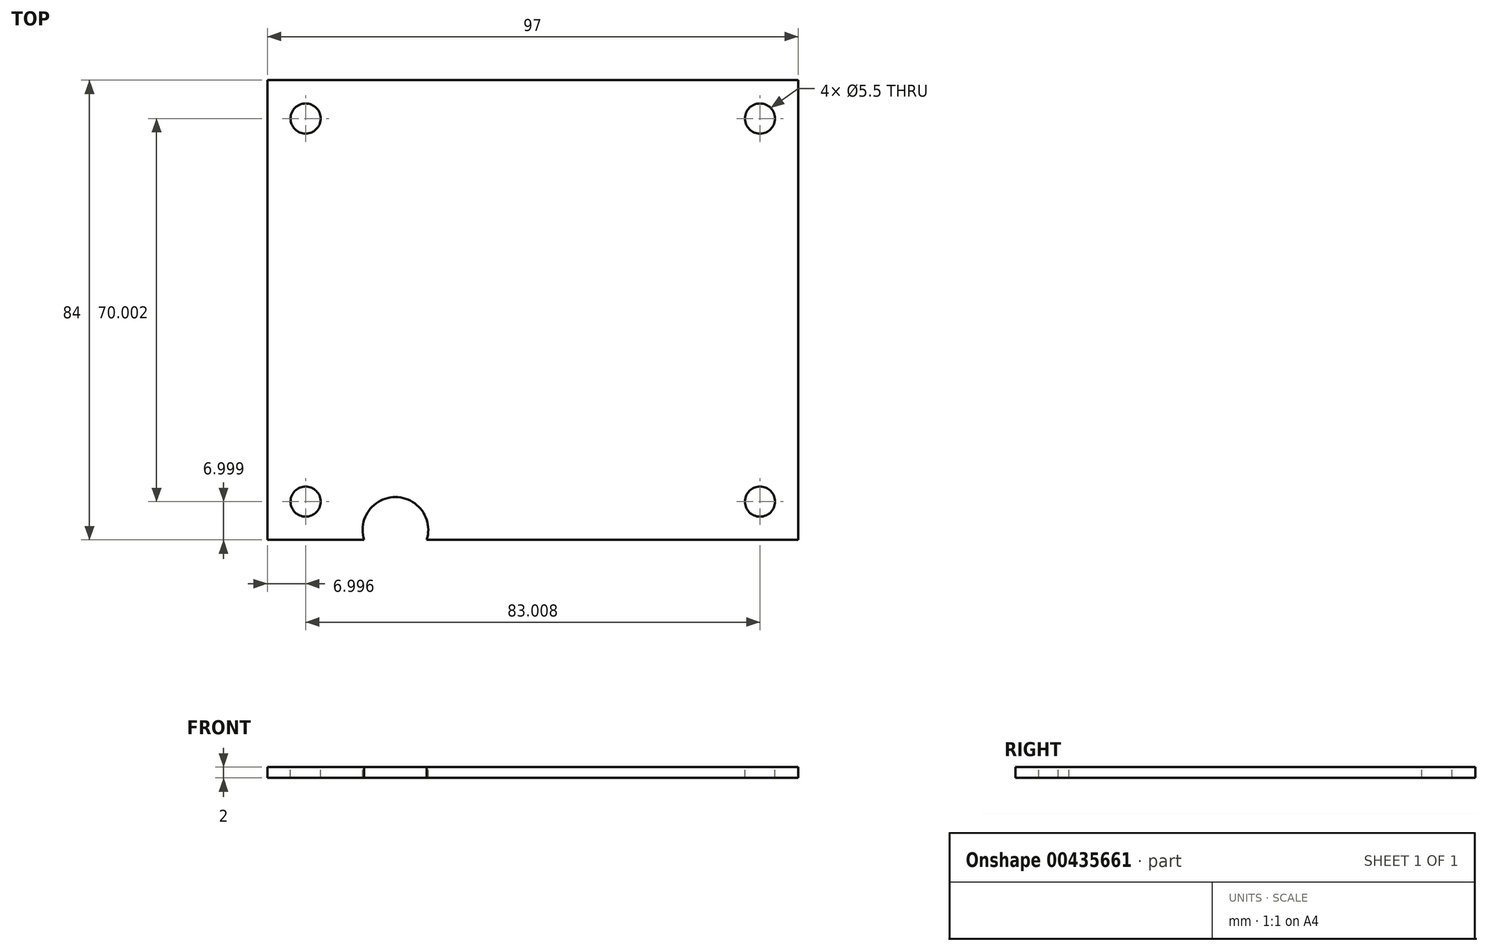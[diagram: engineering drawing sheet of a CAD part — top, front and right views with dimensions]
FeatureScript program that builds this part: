
annotation { "Feature Type Name" : "Feature", "Feature Type Description" : "" }
export const myFeature = defineFeature(function(context is Context, id is Id, definition is map)
    precondition{}
    {
        {
            var Q0;
            Q0=qCreatedBy(makeId("Top.planeOp"),FACE);
            var sketch = newSketch(context, id + "F0", { "sketchPlane" : qUnion([Q0])});
            skLineSegment(sketch, "E0.bottom", {"start": v(-48.5, 42) * mm, "end": v(48.5, 42) * mm});
            skLineSegment(sketch, "E0.top", {"start": v(-48.5, -42) * mm, "end": v(48.5, -42) * mm});
            skLineSegment(sketch, "E0.left", {"start": v(-48.5, 42) * mm, "end": v(-48.5, -42) * mm});
            skLineSegment(sketch, "E0.right", {"start": v(48.5, 42) * mm, "end": v(48.5, -42) * mm});
            skLineSegment(sketch, "E1", {"start": v(-48.5, 42) * mm, "end": v(48.5, -42) * mm, "construction": true});
            skSolve(sketch);
        }
        {
            var Q0;
            Q0=makeQuery(id+"F0.imprint","IMPRINT",FACE,{"disambiguationData":[TD([[makeQuery(id+"F0.imprint","IMPRINT",EDGE,{"derivedFrom":sQuery(id+"F0.wireOp",EDGE,"E0.bottom")}),-1.0]])]});
            extrude(context, id + "F1", {"entities" : qUnion([Q0]), "depth" : 2 * mm});
        }
        {
            var Q0;
            Q0=makeQuery(id+"F1.opExtrude","CAP_FACE",FACE,{"disambiguationData":[OSD([sQuery(id+"F0.wireOp",EDGE,"E0.bottom"),sQuery(id+"F0.wireOp",EDGE,"E0.top"),sQuery(id+"F0.wireOp",EDGE,"E0.left"),sQuery(id+"F0.wireOp",EDGE,"E0.right")])],"isStart":false});
            var sketch = newSketch(context, id + "F2", { "sketchPlane" : qUnion([Q0])});
            skCircle(sketch, "E2", {"center": v(-41.5, 35) * mm, "radius": 2.75 * mm});
            skCircle(sketch, "E3", {"center": v(41.5, 35) * mm, "radius": 2.75 * mm});
            skCircle(sketch, "E4", {"center": v(41.5, -35) * mm, "radius": 2.75 * mm});
            skCircle(sketch, "E5", {"center": v(-41.5, -35) * mm, "radius": 2.75 * mm});
            skLineSegment(sketch, "E6", {"start": v(-41.5, 35) * mm, "end": v(41.5, -35) * mm, "construction": true});
            skLineSegment(sketch, "E7", {"start": v(-41.5, -35) * mm, "end": v(41.5, 35) * mm, "construction": true});
            skSolve(sketch);
        }
        {
            var Q0;
            Q0=qSketchRegion(id+"F2",true);
            extrude(context, id + "F3", {"entities" : qUnion([Q0]), "operationType" : NewBodyOperationType.REMOVE, "endBound" : BoundingType.UP_TO_NEXT, "oppositeDirection" : true, "depth" : 25.4 * mm});
        }
        {
            var Q0;
            Q0=makeQuery(id+"F1.opExtrude","CAP_FACE",FACE,{"disambiguationData":[OSD([sQuery(id+"F0.wireOp",EDGE,"E0.bottom"),sQuery(id+"F0.wireOp",EDGE,"E0.top"),sQuery(id+"F0.wireOp",EDGE,"E0.left"),sQuery(id+"F0.wireOp",EDGE,"E0.right")])],"isStart":false});
            var sketch = newSketch(context, id + "F4", { "sketchPlane" : qUnion([Q0])});
            skArc(sketch, "E8", {"start": v(-19.38, -42) * mm, "mid": v(-25.1, -34.18) * mm, "end": v(-30.82, -42) * mm});
            skLineSegment(sketch, "E9", {"start": v(-30.82, -42) * mm, "end": v(-19.38, -42) * mm});
            skSolve(sketch);
        }
        {
            var Q0;
            Q0=qSketchRegion(id+"F4",true);
            extrude(context, id + "F5", {"entities" : qUnion([Q0]), "operationType" : NewBodyOperationType.REMOVE, "endBound" : BoundingType.UP_TO_NEXT, "oppositeDirection" : true, "depth" : 25.4 * mm});
        }
    });
